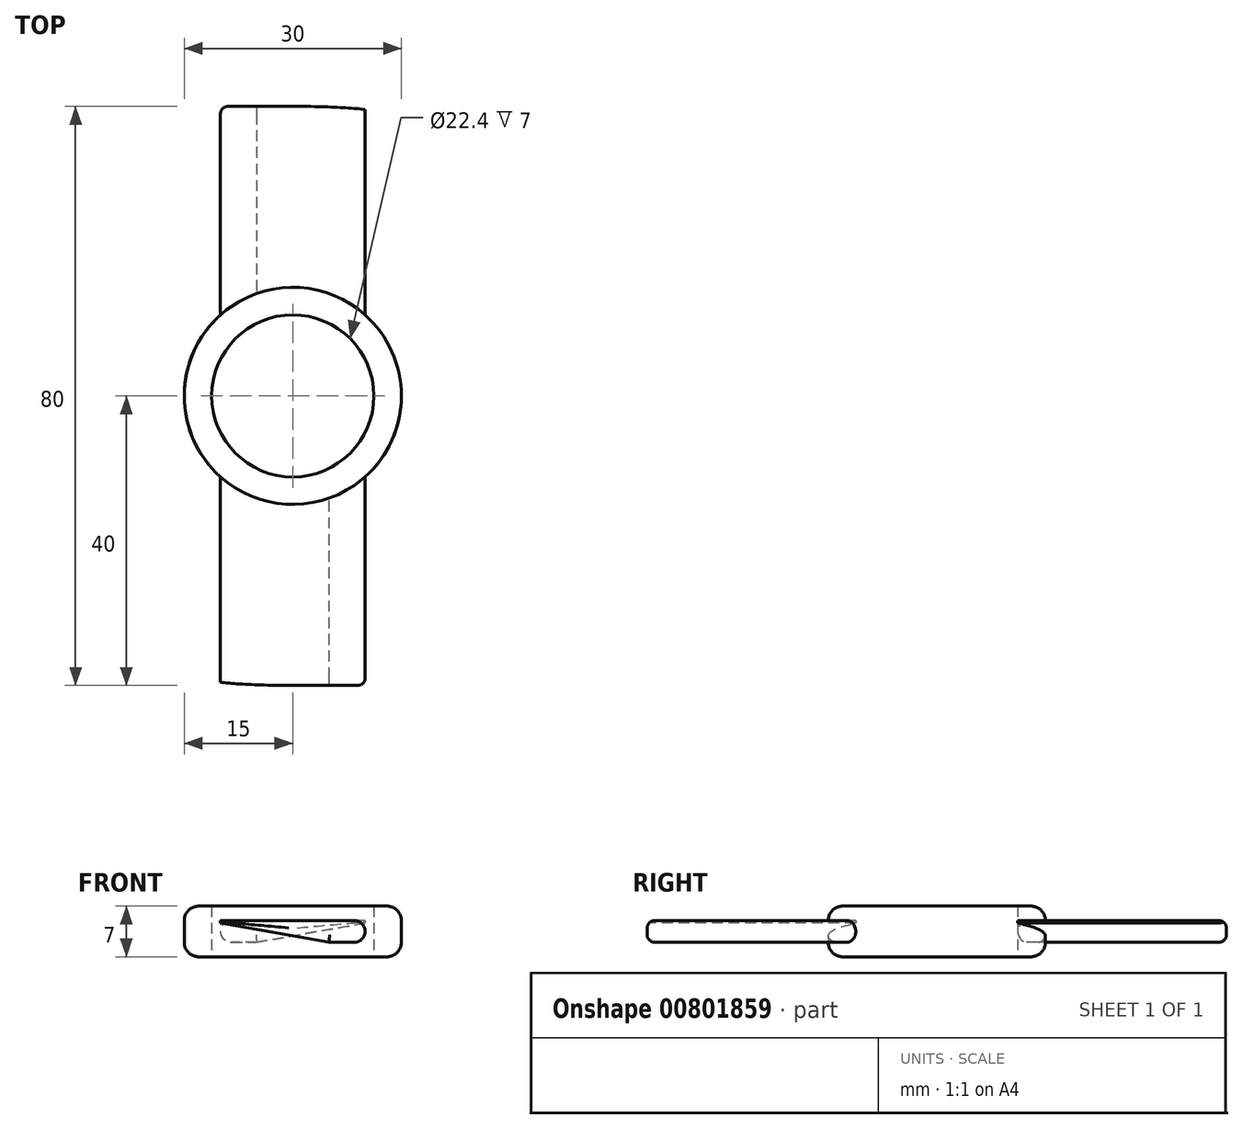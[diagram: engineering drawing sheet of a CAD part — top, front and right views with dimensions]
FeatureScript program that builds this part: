
annotation { "Feature Type Name" : "Feature", "Feature Type Description" : "" }
export const myFeature = defineFeature(function(context is Context, id is Id, definition is map)
    precondition{}
    {
        {
            var Q0;
            Q0=qCreatedBy(makeId("Top.planeOp"),FACE);
            var sketch = newSketch(context, id + "F0", { "sketchPlane" : qUnion([Q0])});
            skCircle(sketch, "E0", {"center": v(0, 0) * mm, "radius": 11.2 * mm});
            skCircle(sketch, "E1", {"center": v(0, 0) * mm, "radius": 15 * mm});
            skLineSegment(sketch, "E2.bottom", {"start": v(-10, 40) * mm, "end": v(10, 40) * mm});
            skLineSegment(sketch, "E2.left", {"start": v(-10, 40) * mm, "end": v(-10, -11.18) * mm});
            skLineSegment(sketch, "E2.right", {"start": v(10, 40) * mm, "end": v(10, -11.18) * mm});
            skPoint(sketch, "E2.top.end.orphan", {"position": v(10, -40) * mm});
            skPoint(sketch, "E3.orphan", {"position": v(-10, -40) * mm});
            skSolve(sketch);
        }
        {
            var Q0;
            {var subQ0=sQuery(id+"F0.wireOp",EDGE,"E2.left");var subQ1=sQuery(id+"F0.wireOp",EDGE,"E0");var subQ2=makeQuery(id+"F0.imprint","INTERSECT",VERTEX,{"disambiguationData":[OD(0.0)],"derivedFrom":[subQ1,subQ0]});Q0=makeQuery(id+"F0.imprint","IMPRINT",FACE,{"disambiguationData":[TD([[makeQuery(id+"F0.imprint","IMPRINT",EDGE,{"disambiguationData":[TD([[subQ2,-1.0]])],"derivedFrom":subQ1}),-1.0]])]});}
            var Q1;
            {var subQ0=sQuery(id+"F0.wireOp",EDGE,"E2.left");var subQ1=sQuery(id+"F0.wireOp",EDGE,"E0");var subQ2=makeQuery(id+"F0.imprint","INTERSECT",VERTEX,{"disambiguationData":[OD(0.0)],"derivedFrom":[subQ1,subQ0]});Q1=makeQuery(id+"F0.imprint","IMPRINT",FACE,{"disambiguationData":[TD([[makeQuery(id+"F0.imprint","IMPRINT",EDGE,{"disambiguationData":[TD([[subQ2,1.0]])],"derivedFrom":subQ1}),-1.0]])]});}
            var Q2;
            {var subQ0=sQuery(id+"F0.wireOp",EDGE,"E2.right");var subQ1=sQuery(id+"F0.wireOp",EDGE,"E0");var subQ2=makeQuery(id+"F0.imprint","INTERSECT",VERTEX,{"disambiguationData":[OD(0.0)],"derivedFrom":[subQ1,subQ0]});Q2=makeQuery(id+"F0.imprint","IMPRINT",FACE,{"disambiguationData":[TD([[makeQuery(id+"F0.imprint","IMPRINT",EDGE,{"disambiguationData":[TD([[subQ2,1.0]])],"derivedFrom":subQ1}),-1.0]])]});}
            var Q3;
            {var subQ0=sQuery(id+"F0.wireOp",EDGE,"E2.left");var subQ1=sQuery(id+"F0.wireOp",EDGE,"E0");var subQ2=makeQuery(id+"F0.imprint","INTERSECT",VERTEX,{"disambiguationData":[OD(1.0)],"derivedFrom":[subQ1,subQ0]});Q3=makeQuery(id+"F0.imprint","IMPRINT",FACE,{"disambiguationData":[TD([[makeQuery(id+"F0.imprint","IMPRINT",EDGE,{"disambiguationData":[TD([[subQ2,-1.0]])],"derivedFrom":subQ1}),-1.0]])]});}
            extrude(context, id + "F1", {"entities" : qUnion([Q0, Q1, Q2, Q3]), "depth" : 3.5 * mm, "offsetDistance" : 25 * mm, "hasSecondDirection" : true, "secondDirectionOppositeDirection" : true, "secondDirectionDepth" : 3.5 * mm});
        }
        {
            var Q0;
            {var subQ5=sQuery(id+"F0.wireOp",EDGE,"E2.bottom");Q0=makeQuery(id+"F0.imprint","IMPRINT",FACE,{"disambiguationData":[TD([[makeQuery(id+"F0.imprint","IMPRINT",EDGE,{"derivedFrom":subQ5}),-1.0]])]});}
            var Q1;
            {var subQ5=sQuery(id+"F0.wireOp",EDGE,"E2.top");Q1=makeQuery(id+"F0.imprint","IMPRINT",FACE,{"disambiguationData":[TD([[makeQuery(id+"F0.imprint","IMPRINT",EDGE,{"derivedFrom":subQ5}),1.0]])]});}
            extrude(context, id + "F2", {"entities" : qUnion([Q0, Q1]), "operationType" : NewBodyOperationType.ADD, "depth" : 1.5 * mm, "offsetDistance" : 25 * mm, "hasSecondDirection" : true, "secondDirectionOppositeDirection" : true, "secondDirectionDepth" : 1.5 * mm});
        }
        {
            var Q0;
            Q0=makeQuery(id+"F1.opExtrude","CAP_EDGE",EDGE,{"disambiguationData":[OSD([sQuery(id+"F0.wireOp",EDGE,"E1")])],"isStart":false});
            var Q1;
            Q1=makeQuery(id+"F1.opExtrude","CAP_EDGE",EDGE,{"disambiguationData":[OSD([sQuery(id+"F0.wireOp",EDGE,"E1")])],"isStart":true});
            fillet(context, id + "F3", {"entities" : qUnion([Q0, Q1]), "radius" : 2 * mm, "tangentPropagation" : true, "allowEdgeOverflow" : false});
        }
        {
            var Q0;
            {var subQ0=sQuery(id+"F0.wireOp",EDGE,"E2.right");Q0=makeQuery(id+"F2.opExtrude","CAP_EDGE",EDGE,{"disambiguationData":[OSD([subQ0]),TDD([makeQuery(id+"F0.imprint","IMPRINT",EDGE,{"disambiguationData":[TD([[makeQuery(id+"F0.imprint","INTERSECT",VERTEX,{"derivedFrom":[sQuery(id+"F0.wireOp",EDGE,"E2.bottom"),subQ0]}),-1.0]])],"derivedFrom":subQ0})])],"isStart":true});}
            chamfer(context, id + "F4", {"entities" : qUnion([Q0]), "chamferType" : ChamferType.OFFSET_ANGLE, "width" : 15 * mm, "oppositeDirection" : false, "angle" : 10 * degree, "tangentPropagation" : true});
        }
        {
            var Q0;
            Q0=makeQuery(id+"F2.opExtrude","CAP_EDGE",EDGE,{"disambiguationData":[OSD([sQuery(id+"F0.wireOp",EDGE,"E2.left")])],"isStart":true});
            var Q1;
            Q1=makeQuery(id+"F2.opExtrude","CAP_EDGE",EDGE,{"disambiguationData":[OSD([sQuery(id+"F0.wireOp",EDGE,"E2.left")])],"isStart":false});
            fillet(context, id + "F5", {"entities" : qUnion([Q0, Q1]), "radius" : 1.5 * mm, "tangentPropagation" : true, "allowEdgeOverflow" : false});
        }
        {
            var Q0;
            Q0=qCreatedBy(makeId("Right.planeOp"),FACE);
            var sketch = newSketch(context, id + "F6", { "sketchPlane" : qUnion([Q0])});
            skLineSegment(sketch, "E4", {"start": v(0, 26.4) * mm, "end": v(0, -26.95) * mm, "construction": true});
            skSolve(sketch);
        }
        {
            var Q0;
            Q0=makeQuery(id+"F2.opExtrude","CAP_EDGE",EDGE,{"disambiguationData":[OSD([sQuery(id+"F0.wireOp",EDGE,"E2.bottom")])],"isStart":true});
            var Q1;
            Q1=makeQuery(id+"F4.opChamfer","BLEND_EDGE",EDGE,{"blendedFrom":[makeQuery(id+"F2.opExtrude","CAP_EDGE",EDGE,{"disambiguationData":[OSD([sQuery(id+"F0.wireOp",EDGE,"E2.right")])],"isStart":true}),makeQuery(id+"F2.opExtrude","SWEPT_FACE",FACE,{"disambiguationData":[OSD([sQuery(id+"F0.wireOp",EDGE,"E2.bottom")])]})],"blendedInto":[makeQuery(id+"F2.opExtrude","SWEPT_FACE",FACE,{"disambiguationData":[OSD([sQuery(id+"F0.wireOp",EDGE,"E2.bottom")])]})]});
            var Q2;
            Q2=makeQuery(id+"F5.opFillet","BLEND_EDGE",EDGE,{"blendedFrom":[makeQuery(id+"F2.opExtrude","CAP_EDGE",EDGE,{"disambiguationData":[OSD([sQuery(id+"F0.wireOp",EDGE,"E2.left")])],"isStart":true}),makeQuery(id+"F2.opExtrude","SWEPT_FACE",FACE,{"disambiguationData":[OSD([sQuery(id+"F0.wireOp",EDGE,"E2.bottom")])]})],"blendedInto":[makeQuery(id+"F2.opExtrude","SWEPT_FACE",FACE,{"disambiguationData":[OSD([sQuery(id+"F0.wireOp",EDGE,"E2.bottom")])]})]});
            fillet(context, id + "F7", {"entities" : qUnion([Q0, Q1, Q2]), "radius" : 1 * mm, "tangentPropagation" : true, "allowEdgeOverflow" : false});
        }
        {
            var Q0;
            Q0=makeQuery(id+"F1.opExtrude","SWEPT_BODY",BODY,{"disambiguationData":[OSD([sQuery(id+"F0.wireOp",EDGE,"E0"),sQuery(id+"F0.wireOp",EDGE,"E1")])]});
            var Q1;
            Q1=sQuery(id+"F6.wireOp",EDGE,"E4");
            circularPattern(context, id + "F8", {"operationType" : NewBodyOperationType.ADD, "entities" : qUnion([Q0]), "axis" : qUnion([Q1]), "angle" : 360 * degree, "instanceCount" : 2, "equalSpace" : true});
        }
    });
